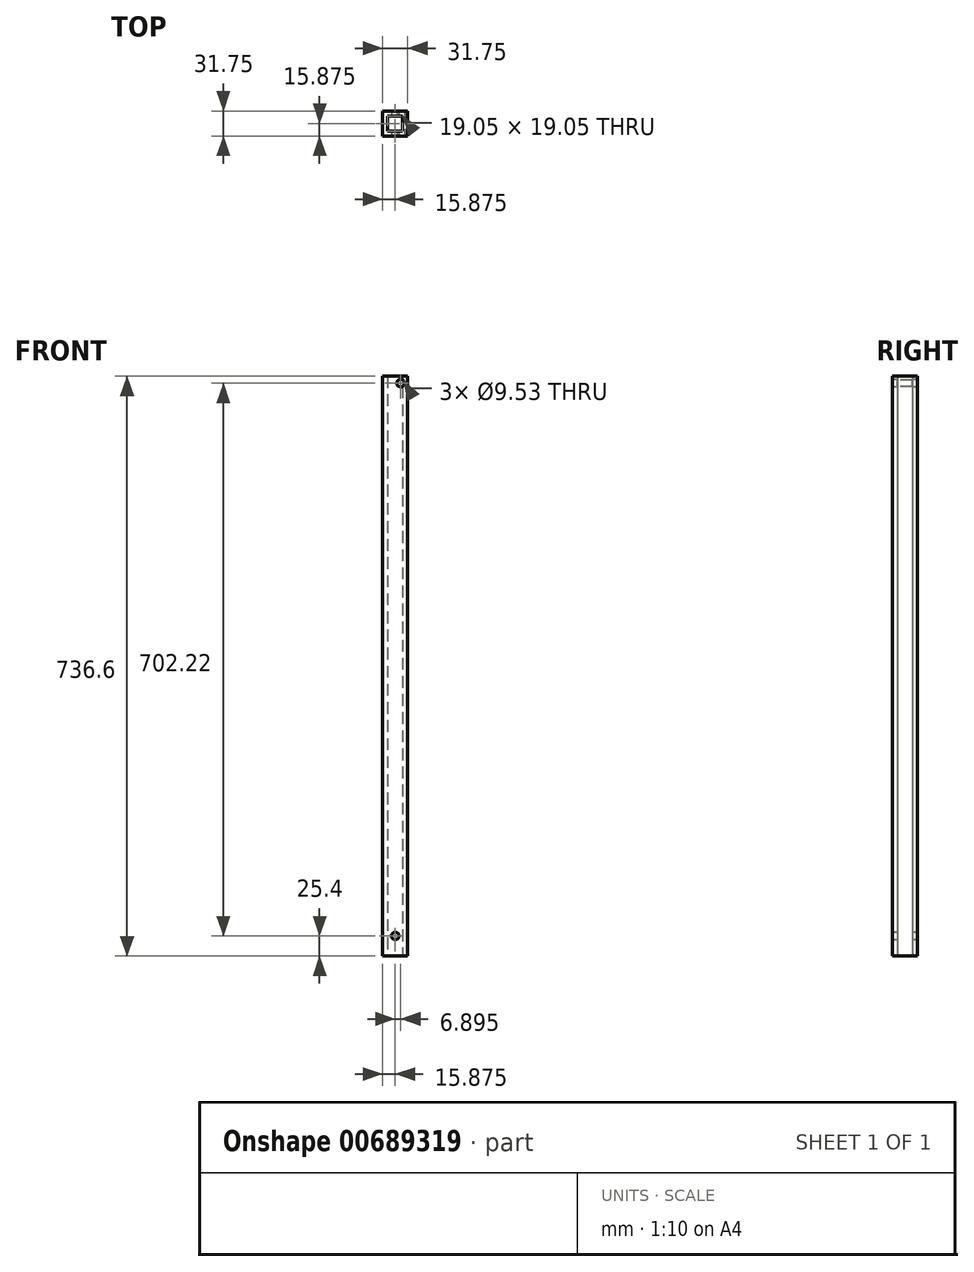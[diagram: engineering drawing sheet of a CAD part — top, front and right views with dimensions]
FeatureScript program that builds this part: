
annotation { "Feature Type Name" : "Feature", "Feature Type Description" : "" }
export const myFeature = defineFeature(function(context is Context, id is Id, definition is map)
    precondition{}
    {
        {
            var Q0;
            Q0=qCreatedBy(makeId("Top.planeOp"),FACE);
            var sketch = newSketch(context, id + "F0", { "sketchPlane" : qUnion([Q0])});
            skLineSegment(sketch, "E0.bottom", {"start": v(0, 0) * mm, "end": v(31.75, 0) * mm});
            skLineSegment(sketch, "E0.top", {"start": v(0, 31.75) * mm, "end": v(31.75, 31.75) * mm});
            skLineSegment(sketch, "E0.left", {"start": v(0, 0) * mm, "end": v(0, 31.75) * mm});
            skLineSegment(sketch, "E0.right", {"start": v(31.75, 0) * mm, "end": v(31.75, 31.75) * mm});
            skLineSegment(sketch, "E1.0", {"start": v(6.35, 6.35) * mm, "end": v(6.35, 25.4) * mm});
            skLineSegment(sketch, "E1.1", {"start": v(6.35, 6.35) * mm, "end": v(25.4, 6.35) * mm});
            skLineSegment(sketch, "E1.2", {"start": v(25.4, 6.35) * mm, "end": v(25.4, 25.4) * mm});
            skLineSegment(sketch, "E1.3", {"start": v(6.35, 25.4) * mm, "end": v(25.4, 25.4) * mm});
            skSolve(sketch);
        }
        {
            var Q0;
            Q0=makeQuery(id+"F0.imprint","IMPRINT",FACE,{"disambiguationData":[TD([[makeQuery(id+"F0.imprint","IMPRINT",EDGE,{"derivedFrom":sQuery(id+"F0.wireOp",EDGE,"E0.bottom")}),1.0]])]});
            extrude(context, id + "F1", {"entities" : qUnion([Q0]), "depth" : 736.6 * mm, "offsetDistance" : 25.4 * mm});
        }
        {
            var Q0;
            Q0=makeQuery(id+"F1.opExtrude","SWEPT_FACE",FACE,{"disambiguationData":[OSD([sQuery(id+"F0.wireOp",EDGE,"E0.bottom")])]});
            var sketch = newSketch(context, id + "F2", { "sketchPlane" : qUnion([Q0])});
            skCircle(sketch, "E2", {"center": v(15.87, 25.4) * mm, "radius": 4.76 * mm});
            skPoint(sketch, "E2.centerSnap0", {"position": v(15.88, 0) * mm});
            skSolve(sketch);
        }
        {
            var Q0;
            Q0=makeQuery(id+"F2.imprint","IMPRINT",FACE,{"disambiguationData":[TD([[makeQuery(id+"F2.imprint","IMPRINT",EDGE,{"derivedFrom":sQuery(id+"F2.wireOp",EDGE,"E2")}),1.0]])]});
            extrude(context, id + "F3", {"entities" : qUnion([Q0]), "operationType" : NewBodyOperationType.REMOVE, "endBound" : BoundingType.THROUGH_ALL, "oppositeDirection" : true, "depth" : 25.4 * mm, "offsetDistance" : 25.4 * mm});
        }
        {
            var Q0;
            Q0=makeQuery(id+"F1.opExtrude","SWEPT_FACE",FACE,{"disambiguationData":[OSD([sQuery(id+"F0.wireOp",EDGE,"E0.bottom")])]});
            var sketch = newSketch(context, id + "F4", { "sketchPlane" : qUnion([Q0])});
            skLineSegment(sketch, "E3", {"start": v(31.75, 736.6) * mm, "end": v(22.77, 727.62) * mm});
            skCircle(sketch, "E4", {"center": v(22.77, 727.62) * mm, "radius": 4.76 * mm});
            skSolve(sketch);
        }
        {
            var Q0;
            Q0=makeQuery(id+"F4.imprint","IMPRINT",FACE,{"disambiguationData":[TD([[makeQuery(id+"F4.imprint","IMPRINT",EDGE,{"derivedFrom":sQuery(id+"F4.wireOp",EDGE,"E4")}),1.0]])]});
            extrude(context, id + "F5", {"entities" : qUnion([Q0]), "operationType" : NewBodyOperationType.REMOVE, "endBound" : BoundingType.THROUGH_ALL, "oppositeDirection" : true, "depth" : 25.4 * mm, "offsetDistance" : 25.4 * mm});
        }
    });
